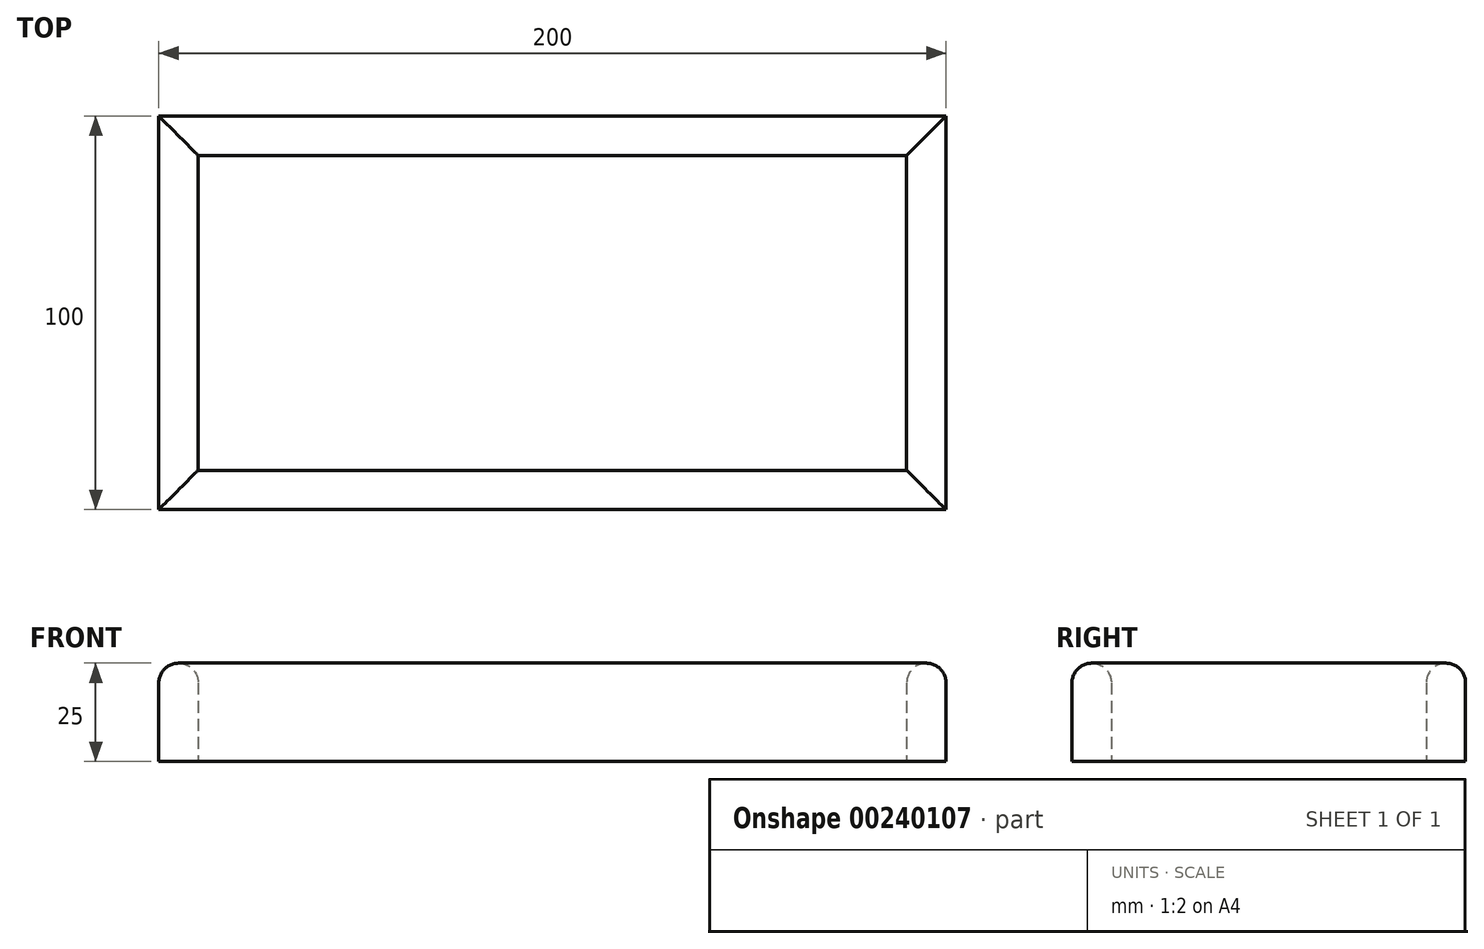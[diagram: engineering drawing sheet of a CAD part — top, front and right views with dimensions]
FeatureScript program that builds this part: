
annotation { "Feature Type Name" : "Feature", "Feature Type Description" : "" }
export const myFeature = defineFeature(function(context is Context, id is Id, definition is map)
    precondition{}
    {
        {
            var Q0;
            Q0=qCreatedBy(makeId("Top.planeOp"),FACE);
            var sketch = newSketch(context, id + "F0", { "sketchPlane" : qUnion([Q0])});
            skLineSegment(sketch, "E0.bottom", {"start": v(100, -50) * mm, "end": v(-100, -50) * mm});
            skLineSegment(sketch, "E0.top", {"start": v(100, 50) * mm, "end": v(-100, 50) * mm});
            skLineSegment(sketch, "E0.left", {"start": v(100, -50) * mm, "end": v(100, 50) * mm});
            skLineSegment(sketch, "E0.right", {"start": v(-100, -50) * mm, "end": v(-100, 50) * mm});
            skPoint(sketch, "E0.middle", {"position": v(0, 0) * mm});
            skLineSegment(sketch, "E1.bottom", {"start": v(90, -40) * mm, "end": v(-90, -40) * mm});
            skLineSegment(sketch, "E1.top", {"start": v(90, 40) * mm, "end": v(-90, 40) * mm});
            skLineSegment(sketch, "E1.left", {"start": v(90, -40) * mm, "end": v(90, 40) * mm});
            skLineSegment(sketch, "E1.right", {"start": v(-90, -40) * mm, "end": v(-90, 40) * mm});
            skSolve(sketch);
        }
        {
            var Q0;
            Q0=makeQuery(id+"F0.imprint","IMPRINT",FACE,{"disambiguationData":[TD([[makeQuery(id+"F0.imprint","IMPRINT",EDGE,{"derivedFrom":sQuery(id+"F0.wireOp",EDGE,"E0.bottom")}),-1.0]])]});
            extrude(context, id + "F1", {"entities" : qUnion([Q0]), "depth" : 25 * mm});
        }
        {
            var Q0;
            Q0=makeQuery(id+"F1.opExtrude","CAP_EDGE",EDGE,{"disambiguationData":[OSD([sQuery(id+"F0.wireOp",EDGE,"E0.right")])],"isStart":false});
            var Q1;
            Q1=makeQuery(id+"F1.opExtrude","CAP_EDGE",EDGE,{"disambiguationData":[OSD([sQuery(id+"F0.wireOp",EDGE,"E0.top")])],"isStart":false});
            var Q2;
            Q2=makeQuery(id+"F1.opExtrude","CAP_FACE",FACE,{"disambiguationData":[OSD([sQuery(id+"F0.wireOp",EDGE,"E0.bottom"),sQuery(id+"F0.wireOp",EDGE,"E0.top"),sQuery(id+"F0.wireOp",EDGE,"E0.left"),sQuery(id+"F0.wireOp",EDGE,"E0.right"),sQuery(id+"F0.wireOp",EDGE,"E1.bottom"),sQuery(id+"F0.wireOp",EDGE,"E1.top"),sQuery(id+"F0.wireOp",EDGE,"E1.left"),sQuery(id+"F0.wireOp",EDGE,"E1.right")])],"isStart":false});
            var Q3;
            Q3=makeQuery(id+"F1.opExtrude","CAP_EDGE",EDGE,{"disambiguationData":[OSD([sQuery(id+"F0.wireOp",EDGE,"E0.bottom")])],"isStart":false});
            fillet(context, id + "F2", {"entities" : qUnion([Q0, Q1, Q2, Q3]), "radius" : 5 * mm, "tangentPropagation" : true, "allowEdgeOverflow" : false});
        }
    });
